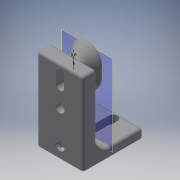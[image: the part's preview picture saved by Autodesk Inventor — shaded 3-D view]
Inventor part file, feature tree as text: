
AUTODESK INVENTOR PART (.ipt)
format: ipt  version: 2016 (Build 200138000, 138)  size: 384,000 bytes
history: native  units: mm
features: sketch x10, extrude x7, projected_geometry x5, plane x3, loft x2, fillet x2, mirror x1, other x1
ambient origin geometry x8: Origin, YZ Plane, XZ Plane, XY Plane, X Axis, Y Axis, Z Axis, Center Point
bodies: Solid1 (feature_tree)
feature tree (31):
  extrude  "Extrusion1"  Depth=3.0mm
  plane  "Work Plane1"
  extrude  "Extrusion3"  Depth=22.0mm
  extrude  "Extrusion4"  Depth=3.3mm
  extrude  "Extrusion6"  Depth=4.0mm TaperAngle=0.0deg
  extrude  "Extrusion7"  Depth=3.3mm
  extrude  "Extrusion8"  Depth=2.5mm
  plane  "Work Plane3"
  loft  "Loft1"
  sketch  "Sketch14"  dims[d29=8.5mm d30=8.5mm d31=1.0mm d32=6.3mm]
  sketch  "Sketch15"  dims[d33=3.0mm d34=9.0mm d35=0.0mm d37=3.5mm d38=7.0mm d39=3.0mm d40=0.0mm d42=4.0mm d43=3.0mm d44=10.0mm d45=0.0mm d49=5.0mm d50=4.5mm d51=0.6mm d52=0.6mm d53=0.0mm d54=90.0deg d55=0.0mm d56=90.0deg d57=0.6mm d58=0.6mm d59=0.0mm d60=90.0deg d61=0.0mm d62=90.0deg d65=1.0mm]
  loft  "Loft2"
  plane  "Work Plane2"
  extrude  "Extrusion5"  Depth=1.0mm
  mirror  "Mirror2"
  fillet  "Fillet2"  Radius=1.0mm
  fillet  "Fillet5"  Radius=6.3mm
  sketch  "Sketch1"  dims[d0=5.0mm d1=3.0mm]
  sketch  "Sketch3"  dims[d2=30.0mm d3=22.0mm]
  sketch  "Sketch4"  dims[d4=17.0mm d5=0.0mm d14=3.3mm]
  projected_geometry  "Projected Loop2"
  sketch  "Sketch5"  dims[d15=3.3mm d16=4.0mm d17=0.0mm]
  sketch  "Sketch6"  dims[d19=12.0mm d20=3.3mm]
  projected_geometry  "Projected Loop4"
  sketch  "Sketch10"  dims[d21=8.0mm d22=0.0mm d23=2.5mm]
  projected_geometry  "Projected Loop5"
  sketch  "Sketch12"  dims[d24=5.0mm d25=4.0mm]
  sketch  "Sketch13"  dims[d26=4.0mm d27=6.0mm d28=0.0mm]
  projected_geometry  "Projected Loop6"
  other  "Edges1"
  projected_geometry  "Project Cut Edges1"
